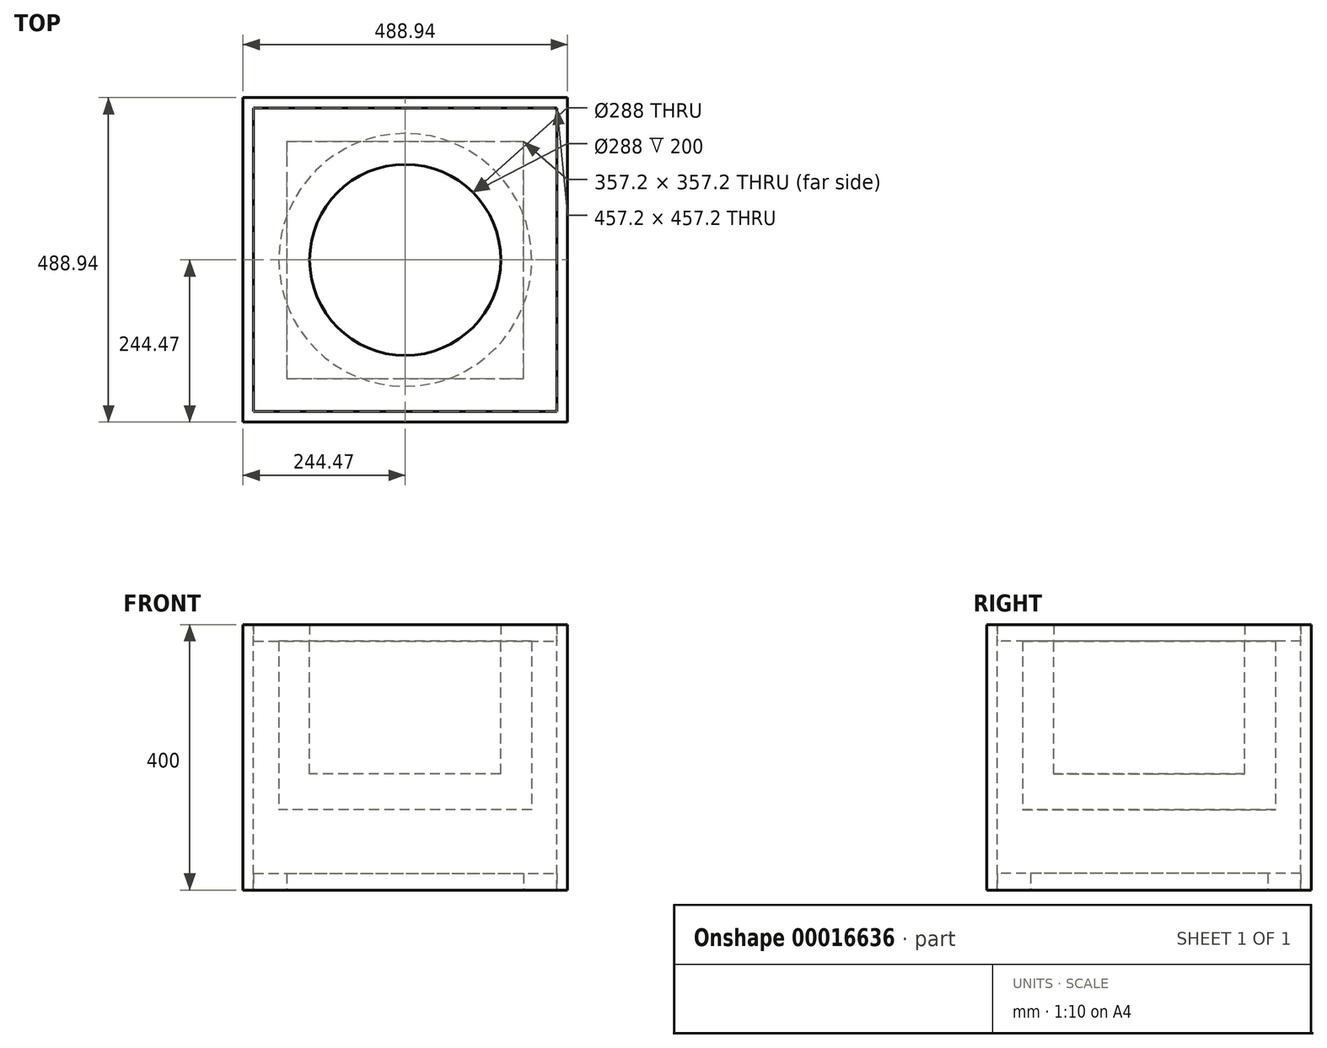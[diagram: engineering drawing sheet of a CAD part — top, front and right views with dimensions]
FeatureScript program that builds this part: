
annotation { "Feature Type Name" : "Feature", "Feature Type Description" : "" }
export const myFeature = defineFeature(function(context is Context, id is Id, definition is map)
    precondition{}
    {
        {
            var Q0;
            Q0=qCreatedBy(makeId("Top.planeOp"),FACE);
            var sketch = newSketch(context, id + "F0", { "sketchPlane" : qUnion([Q0])});
            skCircle(sketch, "E0", {"center": v(0, 0) * mm, "radius": 190.5 * mm});
            skSolve(sketch);
        }
        {
            var Q0;
            Q0 = qSketchRegion(id + "F0", true);
            extrude(context, id + "F1", {"entities" : qUnion([Q0]), "depth" : 254 * mm, "offsetDistance" : 25 * mm});
        }
        {
            var Q0;
            Q0=makeQuery(id+"F1.opExtrude","CAP_FACE",FACE,{"disambiguationData":[OSD([sQuery(id+"F0.wireOp",EDGE,"E0")])],"isStart":false});
            var sketch = newSketch(context, id + "F2", { "sketchPlane" : qUnion([Q0])});
            skCircle(sketch, "E1", {"center": v(0, 0) * mm, "radius": 144 * mm});
            skLineSegment(sketch, "E2.bottom", {"start": v(-228.6, 228.6) * mm, "end": v(228.6, 228.6) * mm});
            skLineSegment(sketch, "E2.top", {"start": v(-228.6, -228.6) * mm, "end": v(228.6, -228.6) * mm});
            skLineSegment(sketch, "E2.left", {"start": v(-228.6, 228.6) * mm, "end": v(-228.6, -228.6) * mm});
            skLineSegment(sketch, "E2.right", {"start": v(228.6, 228.6) * mm, "end": v(228.6, -228.6) * mm});
            skSolve(sketch);
        }
        {
            var Q0;
            Q0 = qSketchRegion(id + "F2", true);
            extrude(context, id + "F3", {"entities" : qUnion([Q0]), "depth" : 25 * mm, "offsetDistance" : 25 * mm});
        }
        {
            var Q0;
            Q0=makeQuery(id+"F1.opExtrude","CAP_FACE",FACE,{"disambiguationData":[OSD([sQuery(id+"F0.wireOp",EDGE,"E0")])],"isStart":false});
            var sketch = newSketch(context, id + "F4", { "sketchPlane" : qUnion([Q0])});
            skCircle(sketch, "E3.0", {"center": v(0, 0) * mm, "radius": 144 * mm});
            skSolve(sketch);
        }
        {
            var Q0;
            Q0 = qSketchRegion(id + "F4", true);
            extrude(context, id + "F5", {"entities" : qUnion([Q0]), "operationType" : NewBodyOperationType.REMOVE, "oppositeDirection" : true, "depth" : 200 * mm, "offsetDistance" : 25 * mm});
        }
        {
            var Q0;
            Q0=makeQuery(id+"F3.opExtrude","CAP_FACE",FACE,{"disambiguationData":[OSD([sQuery(id+"F2.wireOp",EDGE,"E1"),sQuery(id+"F2.wireOp",EDGE,"E2.bottom"),sQuery(id+"F2.wireOp",EDGE,"E2.top"),sQuery(id+"F2.wireOp",EDGE,"E2.left"),sQuery(id+"F2.wireOp",EDGE,"E2.right")])],"isStart":false});
            var sketch = newSketch(context, id + "F6", { "sketchPlane" : qUnion([Q0])});
            skLineSegment(sketch, "E4.0", {"start": v(-228.6, 228.6) * mm, "end": v(-228.6, -228.6) * mm});
            skLineSegment(sketch, "E5.0", {"start": v(-228.6, 228.6) * mm, "end": v(228.6, 228.6) * mm});
            skLineSegment(sketch, "E6.0", {"start": v(228.6, 228.6) * mm, "end": v(228.6, -228.6) * mm});
            skLineSegment(sketch, "E7.0", {"start": v(-228.6, -228.6) * mm, "end": v(228.6, -228.6) * mm});
            skLineSegment(sketch, "E8", {"start": v(-244.47, -244.48) * mm, "end": v(-244.48, 244.48) * mm});
            skLineSegment(sketch, "E9", {"start": v(-244.48, 244.48) * mm, "end": v(244.47, 244.48) * mm});
            skLineSegment(sketch, "E10", {"start": v(244.47, 244.48) * mm, "end": v(244.48, -244.47) * mm});
            skLineSegment(sketch, "E11", {"start": v(244.48, -244.47) * mm, "end": v(-244.47, -244.48) * mm});
            skSolve(sketch);
        }
        {
            var Q0;
            Q0 = qSketchRegion(id + "F6", true);
            extrude(context, id + "F7", {"entities" : qUnion([Q0]), "oppositeDirection" : true, "depth" : 400 * mm, "offsetDistance" : 25 * mm});
        }
        {
            var Q0;
            Q0=makeQuery(id+"F7.opExtrude","CAP_FACE",FACE,{"disambiguationData":[OSD([sQuery(id+"F6.wireOp",EDGE,"E4.0"),sQuery(id+"F6.wireOp",EDGE,"E5.0"),sQuery(id+"F6.wireOp",EDGE,"E6.0"),sQuery(id+"F6.wireOp",EDGE,"E7.0"),sQuery(id+"F6.wireOp",EDGE,"E8"),sQuery(id+"F6.wireOp",EDGE,"E9"),sQuery(id+"F6.wireOp",EDGE,"E10"),sQuery(id+"F6.wireOp",EDGE,"E11")])],"isStart":false});
            var sketch = newSketch(context, id + "F8", { "sketchPlane" : qUnion([Q0])});
            skLineSegment(sketch, "E12.0", {"start": v(-228.6, -228.6) * mm, "end": v(-228.6, 228.6) * mm});
            skLineSegment(sketch, "E13.0", {"start": v(-228.6, 228.6) * mm, "end": v(228.6, 228.6) * mm});
            skLineSegment(sketch, "E14.0", {"start": v(228.6, -228.6) * mm, "end": v(228.6, 228.6) * mm});
            skLineSegment(sketch, "E15.0", {"start": v(-228.6, -228.6) * mm, "end": v(228.6, -228.6) * mm});
            skLineSegment(sketch, "E16.0", {"start": v(-178.6, -178.6) * mm, "end": v(178.6, -178.6) * mm});
            skLineSegment(sketch, "E17", {"start": v(-178.6, -178.6) * mm, "end": v(-178.6, 178.6) * mm});
            skLineSegment(sketch, "E18", {"start": v(-178.6, 178.6) * mm, "end": v(178.6, 178.6) * mm});
            skLineSegment(sketch, "E19", {"start": v(178.6, 178.6) * mm, "end": v(178.6, -178.6) * mm});
            skSolve(sketch);
        }
        {
            var Q0;
            Q0 = qSketchRegion(id + "F8", true);
            extrude(context, id + "F9", {"entities" : qUnion([Q0]), "oppositeDirection" : true, "depth" : 25 * mm, "offsetDistance" : 25 * mm});
        }
    });
